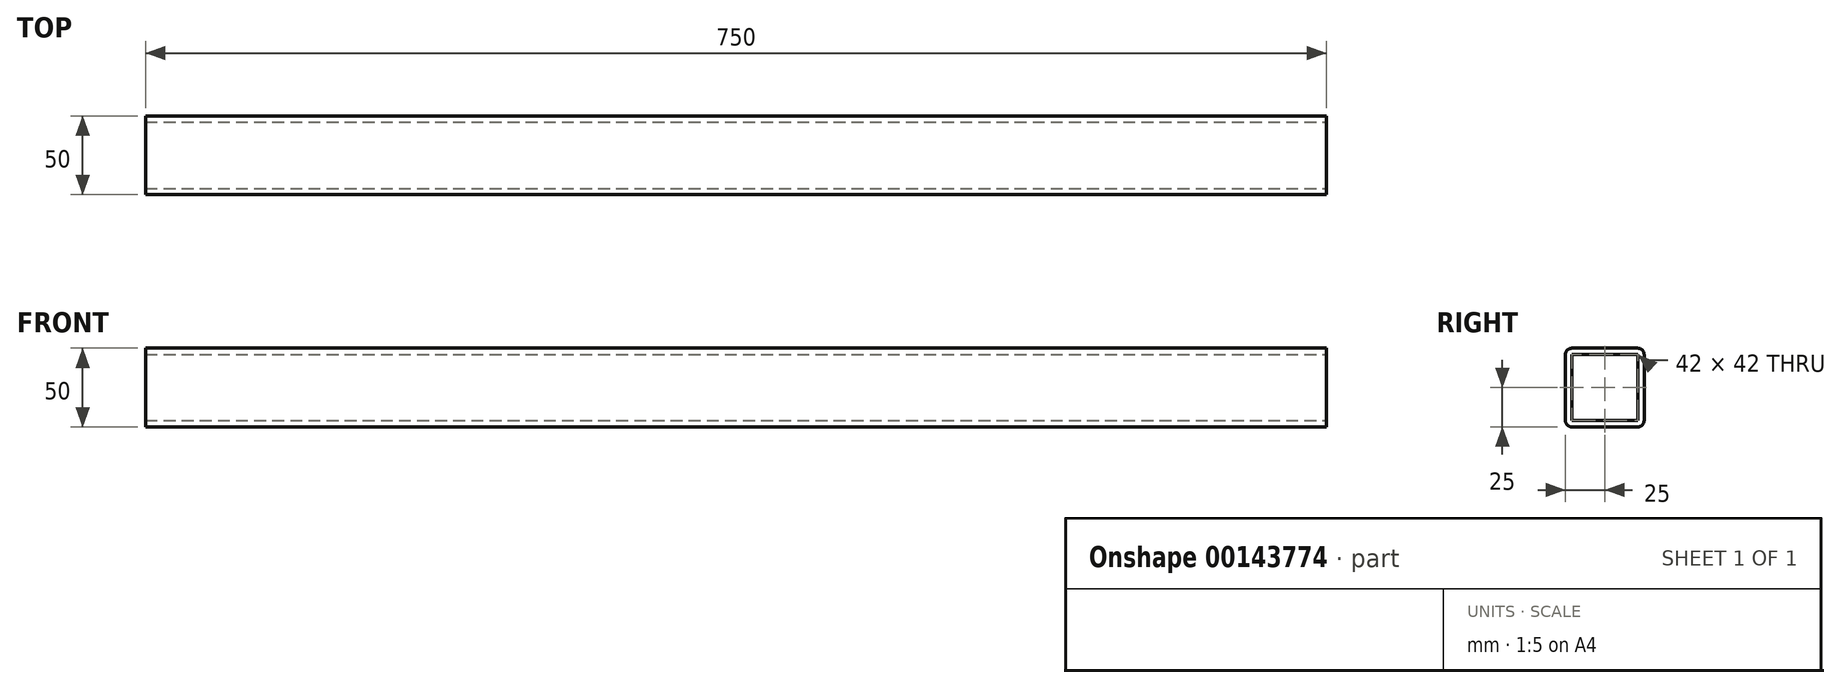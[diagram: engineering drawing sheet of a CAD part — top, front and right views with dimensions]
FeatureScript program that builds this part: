
annotation { "Feature Type Name" : "Feature", "Feature Type Description" : "" }
export const myFeature = defineFeature(function(context is Context, id is Id, definition is map)
    precondition{}
    {
        {
            var Q0;
            Q0=qCreatedBy(makeId("Right.planeOp"),FACE);
            var sketch = newSketch(context, id + "F0", { "sketchPlane" : qUnion([Q0])});
            skLineSegment(sketch, "E0.bottom", {"start": v(-21, 25) * mm, "end": v(21, 25) * mm});
            skLineSegment(sketch, "E0.top", {"start": v(-21, -25) * mm, "end": v(21, -25) * mm});
            skLineSegment(sketch, "E0.left", {"start": v(-25, 21) * mm, "end": v(-25, -21) * mm});
            skLineSegment(sketch, "E0.right", {"start": v(25, 21) * mm, "end": v(25, -21) * mm});
            skPoint(sketch, "E1.visualSharp", {"position": v(-25, 25) * mm});
            skArc(sketch, "E1.filletArc", {"start": v(-21, 25) * mm, "mid": v(-23.83, 23.83) * mm, "end": v(-25, 21) * mm});
            skPoint(sketch, "E2.visualSharp", {"position": v(-25, -25) * mm});
            skArc(sketch, "E2.filletArc", {"start": v(-25, -21) * mm, "mid": v(-23.83, -23.83) * mm, "end": v(-21, -25) * mm});
            skPoint(sketch, "E3.visualSharp", {"position": v(25, -25) * mm});
            skArc(sketch, "E3.filletArc", {"start": v(21, -25) * mm, "mid": v(23.83, -23.83) * mm, "end": v(25, -21) * mm});
            skPoint(sketch, "E4.visualSharp", {"position": v(25, 25) * mm});
            skArc(sketch, "E4.filletArc", {"start": v(25, 21) * mm, "mid": v(23.83, 23.83) * mm, "end": v(21, 25) * mm});
            skLineSegment(sketch, "E5.0", {"start": v(21, 21) * mm, "end": v(21, -21) * mm});
            skLineSegment(sketch, "E5.1", {"start": v(-21, 21) * mm, "end": v(21, 21) * mm});
            skLineSegment(sketch, "E5.2", {"start": v(-21, 21) * mm, "end": v(-21, -21) * mm});
            skLineSegment(sketch, "E5.3", {"start": v(-21, -21) * mm, "end": v(21, -21) * mm});
            skSolve(sketch);
        }
        {
            var Q0;
            Q0=makeQuery(id+"F0.imprint","IMPRINT",FACE,{"disambiguationData":[TD([[makeQuery(id+"F0.imprint","IMPRINT",EDGE,{"derivedFrom":sQuery(id+"F0.wireOp",EDGE,"E0.bottom")}),-1.0]])]});
            extrude(context, id + "F1", {"entities" : qUnion([Q0]), "endBound" : BoundingType.SYMMETRIC, "oppositeDirection" : true, "depth" : 750 * mm});
        }
    });
